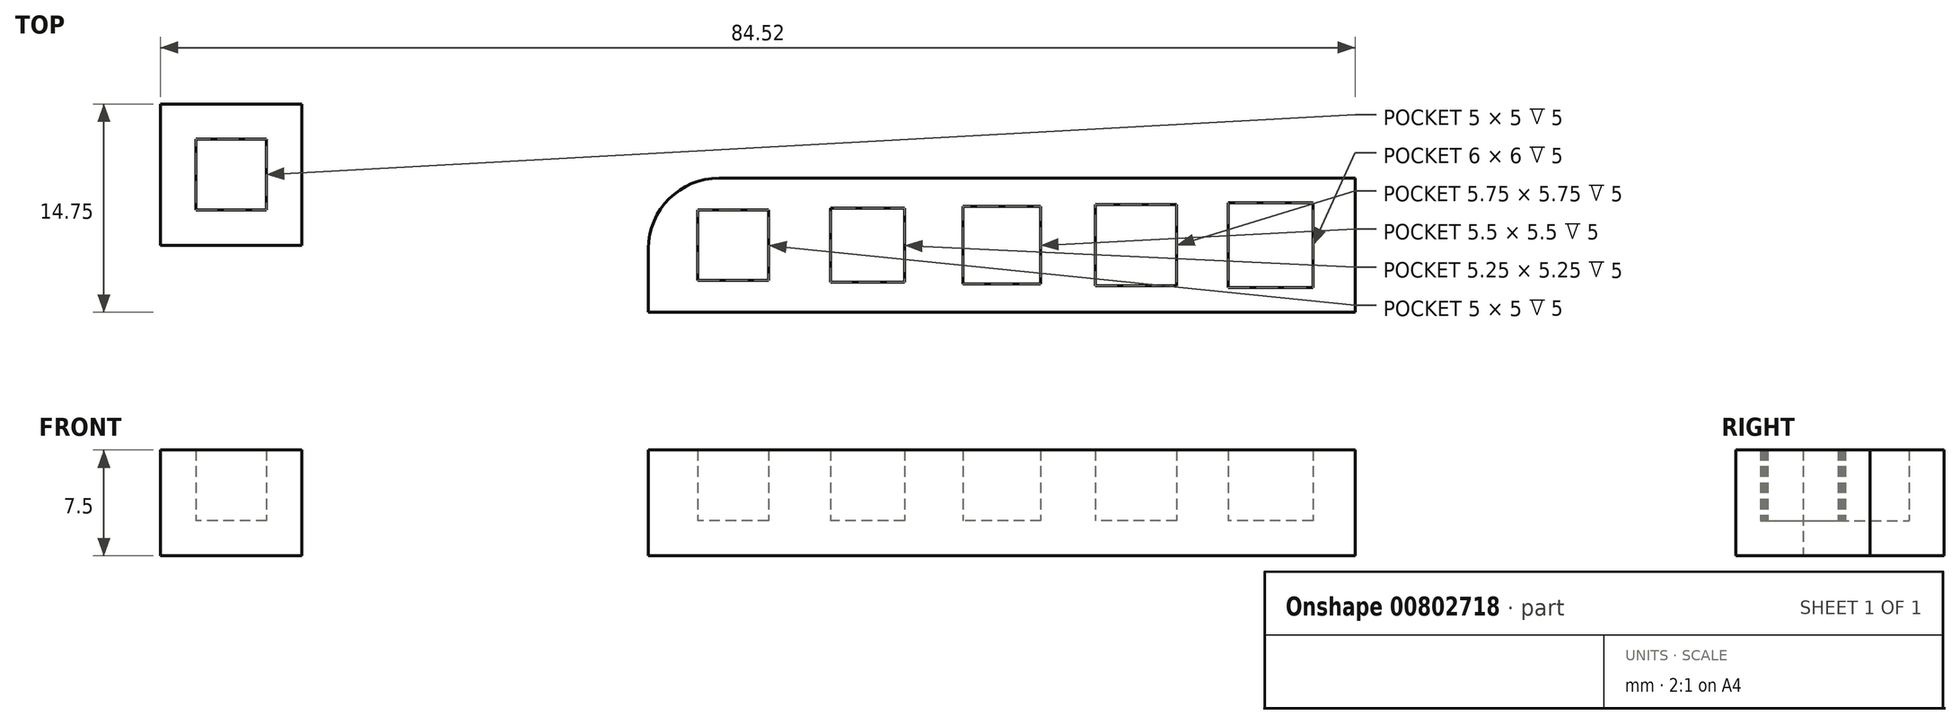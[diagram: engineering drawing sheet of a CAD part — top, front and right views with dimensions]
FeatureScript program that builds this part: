
annotation { "Feature Type Name" : "Feature", "Feature Type Description" : "" }
export const myFeature = defineFeature(function(context is Context, id is Id, definition is map)
    precondition{}
    {
        {
            var Q0;
            Q0=qCreatedBy(makeId("Top.planeOp"),FACE);
            var sketch = newSketch(context, id + "F0", { "sketchPlane" : qUnion([Q0])});
            skLineSegment(sketch, "E0.bottom", {"start": v(2.5, -2.5) * mm, "end": v(-2.5, -2.5) * mm});
            skLineSegment(sketch, "E0.top", {"start": v(2.5, 2.5) * mm, "end": v(-2.5, 2.5) * mm});
            skLineSegment(sketch, "E0.left", {"start": v(2.5, -2.5) * mm, "end": v(2.5, 2.5) * mm});
            skLineSegment(sketch, "E0.right", {"start": v(-2.5, -2.5) * mm, "end": v(-2.5, 2.5) * mm});
            skPoint(sketch, "E0.middle", {"position": v(0, 0) * mm});
            skLineSegment(sketch, "E1.bottom", {"start": v(12.12, -2.63) * mm, "end": v(6.87, -2.63) * mm});
            skLineSegment(sketch, "E1.top", {"start": v(12.12, 2.62) * mm, "end": v(6.87, 2.62) * mm});
            skLineSegment(sketch, "E1.left", {"start": v(12.12, -2.63) * mm, "end": v(12.12, 2.62) * mm});
            skLineSegment(sketch, "E1.right", {"start": v(6.87, -2.63) * mm, "end": v(6.87, 2.62) * mm});
            skPoint(sketch, "E1.middle", {"position": v(9.5, 0) * mm});
            skLineSegment(sketch, "E2.bottom", {"start": v(21.75, -2.75) * mm, "end": v(16.25, -2.75) * mm});
            skLineSegment(sketch, "E2.top", {"start": v(21.75, 2.75) * mm, "end": v(16.25, 2.75) * mm});
            skLineSegment(sketch, "E2.left", {"start": v(21.75, -2.75) * mm, "end": v(21.75, 2.75) * mm});
            skLineSegment(sketch, "E2.right", {"start": v(16.25, -2.75) * mm, "end": v(16.25, 2.75) * mm});
            skPoint(sketch, "E2.middle", {"position": v(19, 0) * mm});
            skLineSegment(sketch, "E3.bottom", {"start": v(31.38, -2.88) * mm, "end": v(25.63, -2.88) * mm});
            skLineSegment(sketch, "E3.top", {"start": v(31.38, 2.87) * mm, "end": v(25.63, 2.87) * mm});
            skLineSegment(sketch, "E3.left", {"start": v(31.38, -2.88) * mm, "end": v(31.38, 2.87) * mm});
            skLineSegment(sketch, "E3.right", {"start": v(25.63, -2.88) * mm, "end": v(25.63, 2.87) * mm});
            skPoint(sketch, "E3.middle", {"position": v(28.5, 0) * mm});
            skLineSegment(sketch, "E4", {"start": v(0, 0) * mm, "end": v(9.5, 0) * mm, "construction": true});
            skLineSegment(sketch, "E5", {"start": v(9.5, 0) * mm, "end": v(19, 0) * mm, "construction": true});
            skLineSegment(sketch, "E6", {"start": v(19, 0) * mm, "end": v(28.5, 0) * mm, "construction": true});
            skLineSegment(sketch, "E7", {"start": v(28.5, 0) * mm, "end": v(38, 0) * mm, "construction": true});
            skLineSegment(sketch, "E8.bottom", {"start": v(41, -3) * mm, "end": v(35, -3) * mm});
            skLineSegment(sketch, "E8.top", {"start": v(41, 3) * mm, "end": v(35, 3) * mm});
            skLineSegment(sketch, "E8.left", {"start": v(41, -3) * mm, "end": v(41, 3) * mm});
            skLineSegment(sketch, "E8.right", {"start": v(35, -3) * mm, "end": v(35, 3) * mm});
            skPoint(sketch, "E8.middle", {"position": v(38, 0) * mm});
            skLineSegment(sketch, "E9.bottom", {"start": v(44, 4.75) * mm, "end": v(-1, 4.75) * mm});
            skLineSegment(sketch, "E9.top", {"start": v(44, -4.75) * mm, "end": v(-6, -4.75) * mm});
            skLineSegment(sketch, "E9.left", {"start": v(44, 4.75) * mm, "end": v(44, -4.75) * mm});
            skLineSegment(sketch, "E9.right", {"start": v(-6, -0.25) * mm, "end": v(-6, -4.75) * mm});
            skLineSegment(sketch, "E10", {"start": v(0, 0) * mm, "end": v(-6, 0) * mm, "construction": true});
            skLineSegment(sketch, "E11", {"start": v(38, 0) * mm, "end": v(44, 0) * mm, "construction": true});
            skPoint(sketch, "E12.visualSharp", {"position": v(-6, 4.75) * mm});
            skArc(sketch, "E12.filletArc", {"start": v(-1, 4.75) * mm, "mid": v(-4.54, 3.29) * mm, "end": v(-6, -0.25) * mm});
            skSolve(sketch);
        }
        {
            var Q0;
            Q0 = qSketchRegion(id + "F0", true);
            extrude(context, id + "F1", {"entities" : qUnion([Q0]), "depth" : 5 * mm, "offsetDistance" : 25 * mm});
        }
        {
            var Q0;
            Q0=makeQuery(id+"F0.imprint","IMPRINT",FACE,{"disambiguationData":[TD([[makeQuery(id+"F0.imprint","IMPRINT",EDGE,{"derivedFrom":sQuery(id+"F0.wireOp",EDGE,"E0.bottom")}),1.0]])]});
            var Q1;
            Q1=makeQuery(id+"F0.imprint","IMPRINT",FACE,{"disambiguationData":[TD([[makeQuery(id+"F0.imprint","IMPRINT",EDGE,{"derivedFrom":sQuery(id+"F0.wireOp",EDGE,"E8.bottom")}),-1.0]])]});
            var Q2;
            Q2=makeQuery(id+"F0.imprint","IMPRINT",FACE,{"disambiguationData":[TD([[makeQuery(id+"F0.imprint","IMPRINT",EDGE,{"derivedFrom":sQuery(id+"F0.wireOp",EDGE,"E3.bottom")}),-1.0]])]});
            var Q3;
            Q3=makeQuery(id+"F0.imprint","IMPRINT",FACE,{"disambiguationData":[TD([[makeQuery(id+"F0.imprint","IMPRINT",EDGE,{"derivedFrom":sQuery(id+"F0.wireOp",EDGE,"E2.bottom")}),-1.0]])]});
            var Q4;
            Q4=makeQuery(id+"F0.imprint","IMPRINT",FACE,{"disambiguationData":[TD([[makeQuery(id+"F0.imprint","IMPRINT",EDGE,{"derivedFrom":sQuery(id+"F0.wireOp",EDGE,"E1.bottom")}),-1.0]])]});
            var Q5;
            Q5=makeQuery(id+"F0.imprint","IMPRINT",FACE,{"disambiguationData":[TD([[makeQuery(id+"F0.imprint","IMPRINT",EDGE,{"derivedFrom":sQuery(id+"F0.wireOp",EDGE,"E0.bottom")}),-1.0]])]});
            extrude(context, id + "F2", {"entities" : qUnion([Q0, Q1, Q2, Q3, Q4, Q5]), "operationType" : NewBodyOperationType.ADD, "oppositeDirection" : true, "depth" : 2.5 * mm, "offsetDistance" : 25 * mm});
        }
        {
            var Q0;
            Q0=qCreatedBy(makeId("Top.planeOp"),FACE);
            var sketch = newSketch(context, id + "F3", { "sketchPlane" : qUnion([Q0])});
            skLineSegment(sketch, "E13.bottom", {"start": v(-30.52, 0) * mm, "end": v(-40.52, 0) * mm});
            skLineSegment(sketch, "E13.top", {"start": v(-30.52, 10) * mm, "end": v(-40.52, 10) * mm});
            skLineSegment(sketch, "E13.left", {"start": v(-30.52, 0) * mm, "end": v(-30.52, 10) * mm});
            skLineSegment(sketch, "E13.right", {"start": v(-40.52, 0) * mm, "end": v(-40.52, 10) * mm});
            skPoint(sketch, "E13.middle", {"position": v(-35.52, 5) * mm});
            skLineSegment(sketch, "E14.bottom", {"start": v(-33.02, 2.5) * mm, "end": v(-38.02, 2.5) * mm});
            skLineSegment(sketch, "E14.top", {"start": v(-33.02, 7.5) * mm, "end": v(-38.02, 7.5) * mm});
            skLineSegment(sketch, "E14.left", {"start": v(-33.02, 2.5) * mm, "end": v(-33.02, 7.5) * mm});
            skLineSegment(sketch, "E14.right", {"start": v(-38.02, 2.5) * mm, "end": v(-38.02, 7.5) * mm});
            skSolve(sketch);
        }
        {
            var Q0;
            Q0=makeQuery(id+"F3.imprint","IMPRINT",FACE,{"disambiguationData":[TD([[makeQuery(id+"F3.imprint","IMPRINT",EDGE,{"derivedFrom":sQuery(id+"F3.wireOp",EDGE,"E13.bottom")}),-1.0]])]});
            extrude(context, id + "F4", {"entities" : qUnion([Q0]), "depth" : 5 * mm, "offsetDistance" : 25 * mm});
        }
        {
            var Q0;
            Q0=makeQuery(id+"F3.imprint","IMPRINT",FACE,{"disambiguationData":[TD([[makeQuery(id+"F3.imprint","IMPRINT",EDGE,{"derivedFrom":sQuery(id+"F3.wireOp",EDGE,"E14.bottom")}),-1.0]])]});
            var Q1;
            Q1=makeQuery(id+"F3.imprint","IMPRINT",FACE,{"disambiguationData":[TD([[makeQuery(id+"F3.imprint","IMPRINT",EDGE,{"derivedFrom":sQuery(id+"F3.wireOp",EDGE,"E13.bottom")}),-1.0]])]});
            extrude(context, id + "F5", {"entities" : qUnion([Q0, Q1]), "operationType" : NewBodyOperationType.ADD, "oppositeDirection" : true, "depth" : 2.5 * mm, "offsetDistance" : 25 * mm});
        }
    });
